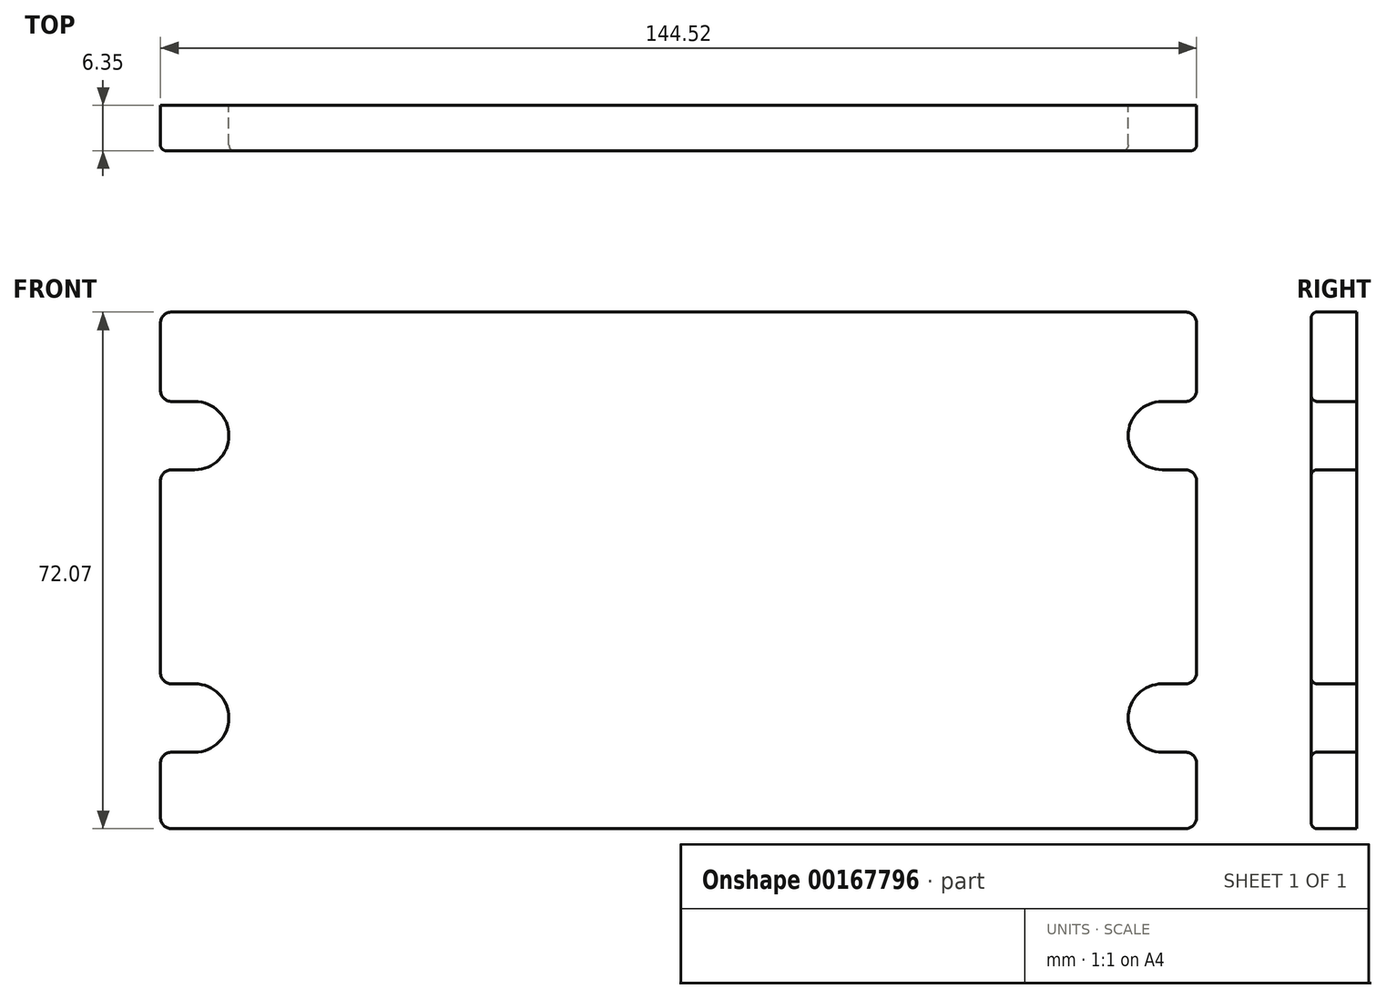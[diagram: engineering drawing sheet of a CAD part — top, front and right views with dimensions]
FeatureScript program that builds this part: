
annotation { "Feature Type Name" : "Feature", "Feature Type Description" : "" }
export const myFeature = defineFeature(function(context is Context, id is Id, definition is map)
    precondition{}
    {
        {
            var Q0;
            Q0=qCreatedBy(makeId("Front.planeOp"),FACE);
            var sketch = newSketch(context, id + "F0", { "sketchPlane" : qUnion([Q0])});
            skLineSegment(sketch, "E0", {"start": v(-72.26, 74.78) * mm, "end": v(-72.26, 65.46) * mm});
            skLineSegment(sketch, "E1", {"start": v(-70.69, 63.88) * mm, "end": v(-67.49, 63.88) * mm});
            skLineSegment(sketch, "E2", {"start": v(-67.49, 54.36) * mm, "end": v(-70.69, 54.36) * mm});
            skLineSegment(sketch, "E3", {"start": v(-72.26, 52.78) * mm, "end": v(-72.26, 26.06) * mm});
            skLineSegment(sketch, "E4", {"start": v(-70.69, 24.49) * mm, "end": v(-67.49, 24.49) * mm});
            skLineSegment(sketch, "E5", {"start": v(-67.49, 14.96) * mm, "end": v(-70.69, 14.96) * mm});
            skLineSegment(sketch, "E6", {"start": v(-72.26, 13.39) * mm, "end": v(-72.26, 5.86) * mm});
            skLineSegment(sketch, "E7", {"start": v(-70.69, 76.36) * mm, "end": v(3.71, 76.36) * mm});
            skLineSegment(sketch, "E8", {"start": v(-70.69, 4.29) * mm, "end": v(0, 4.29) * mm});
            skArc(sketch, "E9", {"start": v(-67.49, 14.96) * mm, "mid": v(-62.73, 19.73) * mm, "end": v(-67.49, 24.49) * mm});
            skArc(sketch, "E10", {"start": v(-67.49, 54.36) * mm, "mid": v(-62.73, 59.12) * mm, "end": v(-67.49, 63.88) * mm});
            skLineSegment(sketch, "E11.MirrorCS", {"start": v(70.69, 76.36) * mm, "end": v(-3.71, 76.36) * mm});
            skLineSegment(sketch, "E12.MirrorCS", {"start": v(70.69, 63.88) * mm, "end": v(67.49, 63.88) * mm});
            skLineSegment(sketch, "E13.MirrorCS", {"start": v(72.26, 52.78) * mm, "end": v(72.26, 26.06) * mm});
            skLineSegment(sketch, "E14.MirrorCS", {"start": v(67.49, 54.36) * mm, "end": v(70.69, 54.36) * mm});
            skLineSegment(sketch, "E15.MirrorCS", {"start": v(72.26, 13.39) * mm, "end": v(72.26, 5.86) * mm});
            skLineSegment(sketch, "E16.MirrorCS", {"start": v(70.69, 24.49) * mm, "end": v(67.49, 24.49) * mm});
            skArc(sketch, "E17.MirrorCS", {"start": v(67.49, 54.36) * mm, "mid": v(62.73, 59.12) * mm, "end": v(67.49, 63.88) * mm});
            skArc(sketch, "E18.MirrorCS", {"start": v(67.49, 14.96) * mm, "mid": v(62.73, 19.73) * mm, "end": v(67.49, 24.49) * mm});
            skLineSegment(sketch, "E19.MirrorCS", {"start": v(72.26, 74.78) * mm, "end": v(72.26, 65.46) * mm});
            skLineSegment(sketch, "E20.MirrorCS", {"start": v(67.49, 14.96) * mm, "end": v(70.69, 14.96) * mm});
            skLineSegment(sketch, "E21.MirrorCS", {"start": v(70.69, 4.29) * mm, "end": v(0, 4.29) * mm});
            skPoint(sketch, "E22.visualSharp", {"position": v(-72.26, 4.29) * mm});
            skArc(sketch, "E22.filletArc", {"start": v(-72.26, 5.86) * mm, "mid": v(-71.8, 4.75) * mm, "end": v(-70.69, 4.29) * mm});
            skPoint(sketch, "E23.visualSharp", {"position": v(-72.26, 14.96) * mm});
            skArc(sketch, "E23.filletArc", {"start": v(-70.69, 14.96) * mm, "mid": v(-71.8, 14.5) * mm, "end": v(-72.26, 13.39) * mm});
            skPoint(sketch, "E24.visualSharp", {"position": v(-72.26, 24.49) * mm});
            skArc(sketch, "E24.filletArc", {"start": v(-72.26, 26.06) * mm, "mid": v(-71.8, 24.95) * mm, "end": v(-70.69, 24.49) * mm});
            skPoint(sketch, "E25.visualSharp", {"position": v(-72.26, 54.36) * mm});
            skArc(sketch, "E25.filletArc", {"start": v(-70.69, 54.36) * mm, "mid": v(-71.8, 53.9) * mm, "end": v(-72.26, 52.78) * mm});
            skPoint(sketch, "E26.visualSharp", {"position": v(-72.26, 63.88) * mm});
            skArc(sketch, "E26.filletArc", {"start": v(-72.26, 65.46) * mm, "mid": v(-71.8, 64.35) * mm, "end": v(-70.69, 63.88) * mm});
            skPoint(sketch, "E27.visualSharp", {"position": v(-72.26, 76.36) * mm});
            skArc(sketch, "E27.filletArc", {"start": v(-70.69, 76.36) * mm, "mid": v(-71.8, 75.9) * mm, "end": v(-72.26, 74.78) * mm});
            skPoint(sketch, "E28.visualSharp", {"position": v(72.26, 76.36) * mm});
            skArc(sketch, "E28.filletArc", {"start": v(72.26, 74.78) * mm, "mid": v(71.8, 75.9) * mm, "end": v(70.69, 76.36) * mm});
            skPoint(sketch, "E29.visualSharp", {"position": v(72.26, 63.88) * mm});
            skArc(sketch, "E29.filletArc", {"start": v(70.69, 63.88) * mm, "mid": v(71.8, 64.35) * mm, "end": v(72.26, 65.46) * mm});
            skPoint(sketch, "E30.visualSharp", {"position": v(72.26, 54.36) * mm});
            skArc(sketch, "E30.filletArc", {"start": v(72.26, 52.78) * mm, "mid": v(71.8, 53.9) * mm, "end": v(70.69, 54.36) * mm});
            skPoint(sketch, "E31.visualSharp", {"position": v(72.26, 24.49) * mm});
            skArc(sketch, "E31.filletArc", {"start": v(70.69, 24.49) * mm, "mid": v(71.8, 24.95) * mm, "end": v(72.26, 26.06) * mm});
            skPoint(sketch, "E32.visualSharp", {"position": v(72.26, 14.96) * mm});
            skArc(sketch, "E32.filletArc", {"start": v(72.26, 13.39) * mm, "mid": v(71.8, 14.5) * mm, "end": v(70.69, 14.96) * mm});
            skPoint(sketch, "E33.visualSharp", {"position": v(72.26, 4.29) * mm});
            skArc(sketch, "E33.filletArc", {"start": v(70.69, 4.29) * mm, "mid": v(71.8, 4.75) * mm, "end": v(72.26, 5.86) * mm});
            skSolve(sketch);
        }
        {
            var Q0;
            Q0=makeQuery(id+"F0.imprint","IMPRINT",FACE,{"disambiguationData":[TD([[makeQuery(id+"F0.imprint","IMPRINT",EDGE,{"derivedFrom":sQuery(id+"F0.wireOp",EDGE,"E0")}),1.0]])]});
            extrude(context, id + "F1", {"entities" : qUnion([Q0]), "depth" : 6.35 * mm});
        }
        {
            var Q0;
            Q0=makeQuery(id+"F1.opExtrude","CAP_EDGE",EDGE,{"disambiguationData":[OSD([sQuery(id+"F0.wireOp",EDGE,"E0")])],"isStart":false});
            var Q1;
            Q1=makeQuery(id+"F1.opExtrude","CAP_EDGE",EDGE,{"disambiguationData":[OSD([sQuery(id+"F0.wireOp",EDGE,"E27.filletArc")])],"isStart":false});
            var Q2;
            Q2=makeQuery(id+"F1.opExtrude","CAP_EDGE",EDGE,{"disambiguationData":[OSD([sQuery(id+"F0.wireOp",EDGE,"E7"),sQuery(id+"F0.wireOp",EDGE,"E11.MirrorCS")])],"isStart":false});
            var Q3;
            Q3=makeQuery(id+"F1.opExtrude","CAP_EDGE",EDGE,{"disambiguationData":[OSD([sQuery(id+"F0.wireOp",EDGE,"E28.filletArc")])],"isStart":false});
            var Q4;
            Q4=makeQuery(id+"F1.opExtrude","CAP_EDGE",EDGE,{"disambiguationData":[OSD([sQuery(id+"F0.wireOp",EDGE,"E19.MirrorCS")])],"isStart":false});
            var Q5;
            Q5=makeQuery(id+"F1.opExtrude","CAP_EDGE",EDGE,{"disambiguationData":[OSD([sQuery(id+"F0.wireOp",EDGE,"E29.filletArc")])],"isStart":false});
            var Q6;
            Q6=makeQuery(id+"F1.opExtrude","CAP_EDGE",EDGE,{"disambiguationData":[OSD([sQuery(id+"F0.wireOp",EDGE,"E17.MirrorCS")])],"isStart":false});
            var Q7;
            Q7=makeQuery(id+"F1.opExtrude","CAP_EDGE",EDGE,{"disambiguationData":[OSD([sQuery(id+"F0.wireOp",EDGE,"E12.MirrorCS")])],"isStart":false});
            var Q8;
            Q8=makeQuery(id+"F1.opExtrude","CAP_EDGE",EDGE,{"disambiguationData":[OSD([sQuery(id+"F0.wireOp",EDGE,"E14.MirrorCS")])],"isStart":false});
            var Q9;
            Q9=makeQuery(id+"F1.opExtrude","CAP_EDGE",EDGE,{"disambiguationData":[OSD([sQuery(id+"F0.wireOp",EDGE,"E30.filletArc")])],"isStart":false});
            var Q10;
            Q10=makeQuery(id+"F1.opExtrude","CAP_EDGE",EDGE,{"disambiguationData":[OSD([sQuery(id+"F0.wireOp",EDGE,"E13.MirrorCS")])],"isStart":false});
            var Q11;
            Q11=makeQuery(id+"F1.opExtrude","CAP_EDGE",EDGE,{"disambiguationData":[OSD([sQuery(id+"F0.wireOp",EDGE,"E31.filletArc")])],"isStart":false});
            var Q12;
            Q12=makeQuery(id+"F1.opExtrude","CAP_EDGE",EDGE,{"disambiguationData":[OSD([sQuery(id+"F0.wireOp",EDGE,"E16.MirrorCS")])],"isStart":false});
            var Q13;
            Q13=makeQuery(id+"F1.opExtrude","CAP_EDGE",EDGE,{"disambiguationData":[OSD([sQuery(id+"F0.wireOp",EDGE,"E18.MirrorCS")])],"isStart":false});
            var Q14;
            Q14=makeQuery(id+"F1.opExtrude","CAP_EDGE",EDGE,{"disambiguationData":[OSD([sQuery(id+"F0.wireOp",EDGE,"E20.MirrorCS")])],"isStart":false});
            var Q15;
            Q15=makeQuery(id+"F1.opExtrude","CAP_EDGE",EDGE,{"disambiguationData":[OSD([sQuery(id+"F0.wireOp",EDGE,"E32.filletArc")])],"isStart":false});
            var Q16;
            Q16=makeQuery(id+"F1.opExtrude","CAP_EDGE",EDGE,{"disambiguationData":[OSD([sQuery(id+"F0.wireOp",EDGE,"E15.MirrorCS")])],"isStart":false});
            var Q17;
            Q17=makeQuery(id+"F1.opExtrude","CAP_EDGE",EDGE,{"disambiguationData":[OSD([sQuery(id+"F0.wireOp",EDGE,"E33.filletArc")])],"isStart":false});
            var Q18;
            Q18=makeQuery(id+"F1.opExtrude","CAP_EDGE",EDGE,{"disambiguationData":[OSD([sQuery(id+"F0.wireOp",EDGE,"E8"),sQuery(id+"F0.wireOp",EDGE,"E21.MirrorCS")])],"isStart":false});
            var Q19;
            Q19=makeQuery(id+"F1.opExtrude","CAP_EDGE",EDGE,{"disambiguationData":[OSD([sQuery(id+"F0.wireOp",EDGE,"E22.filletArc")])],"isStart":false});
            var Q20;
            Q20=makeQuery(id+"F1.opExtrude","CAP_EDGE",EDGE,{"disambiguationData":[OSD([sQuery(id+"F0.wireOp",EDGE,"E6")])],"isStart":false});
            var Q21;
            Q21=makeQuery(id+"F1.opExtrude","CAP_EDGE",EDGE,{"disambiguationData":[OSD([sQuery(id+"F0.wireOp",EDGE,"E23.filletArc")])],"isStart":false});
            var Q22;
            Q22=makeQuery(id+"F1.opExtrude","CAP_EDGE",EDGE,{"disambiguationData":[OSD([sQuery(id+"F0.wireOp",EDGE,"E9")])],"isStart":false});
            var Q23;
            Q23=makeQuery(id+"F1.opExtrude","CAP_EDGE",EDGE,{"disambiguationData":[OSD([sQuery(id+"F0.wireOp",EDGE,"E5")])],"isStart":false});
            var Q24;
            Q24=makeQuery(id+"F1.opExtrude","CAP_EDGE",EDGE,{"disambiguationData":[OSD([sQuery(id+"F0.wireOp",EDGE,"E4")])],"isStart":false});
            var Q25;
            Q25=makeQuery(id+"F1.opExtrude","CAP_EDGE",EDGE,{"disambiguationData":[OSD([sQuery(id+"F0.wireOp",EDGE,"E24.filletArc")])],"isStart":false});
            var Q26;
            Q26=makeQuery(id+"F1.opExtrude","CAP_EDGE",EDGE,{"disambiguationData":[OSD([sQuery(id+"F0.wireOp",EDGE,"E3")])],"isStart":false});
            var Q27;
            Q27=makeQuery(id+"F1.opExtrude","CAP_EDGE",EDGE,{"disambiguationData":[OSD([sQuery(id+"F0.wireOp",EDGE,"E25.filletArc")])],"isStart":false});
            var Q28;
            Q28=makeQuery(id+"F1.opExtrude","CAP_EDGE",EDGE,{"disambiguationData":[OSD([sQuery(id+"F0.wireOp",EDGE,"E10")])],"isStart":false});
            var Q29;
            Q29=makeQuery(id+"F1.opExtrude","CAP_EDGE",EDGE,{"disambiguationData":[OSD([sQuery(id+"F0.wireOp",EDGE,"E2")])],"isStart":false});
            var Q30;
            Q30=makeQuery(id+"F1.opExtrude","CAP_EDGE",EDGE,{"disambiguationData":[OSD([sQuery(id+"F0.wireOp",EDGE,"E1")])],"isStart":false});
            var Q31;
            Q31=makeQuery(id+"F1.opExtrude","CAP_EDGE",EDGE,{"disambiguationData":[OSD([sQuery(id+"F0.wireOp",EDGE,"E26.filletArc")])],"isStart":false});
            fillet(context, id + "F2", {"entities" : qUnion([Q0, Q1, Q2, Q3, Q4, Q5, Q6, Q7, Q8, Q9, Q10, Q11, Q12, Q13, Q14, Q15, Q16, Q17, Q18, Q19, Q20, Q21, Q22, Q23, Q24, Q25, Q26, Q27, Q28, Q29, Q30, Q31]), "radius" : 0.81 * mm, "tangentPropagation" : true, "allowEdgeOverflow" : false});
        }
    });
